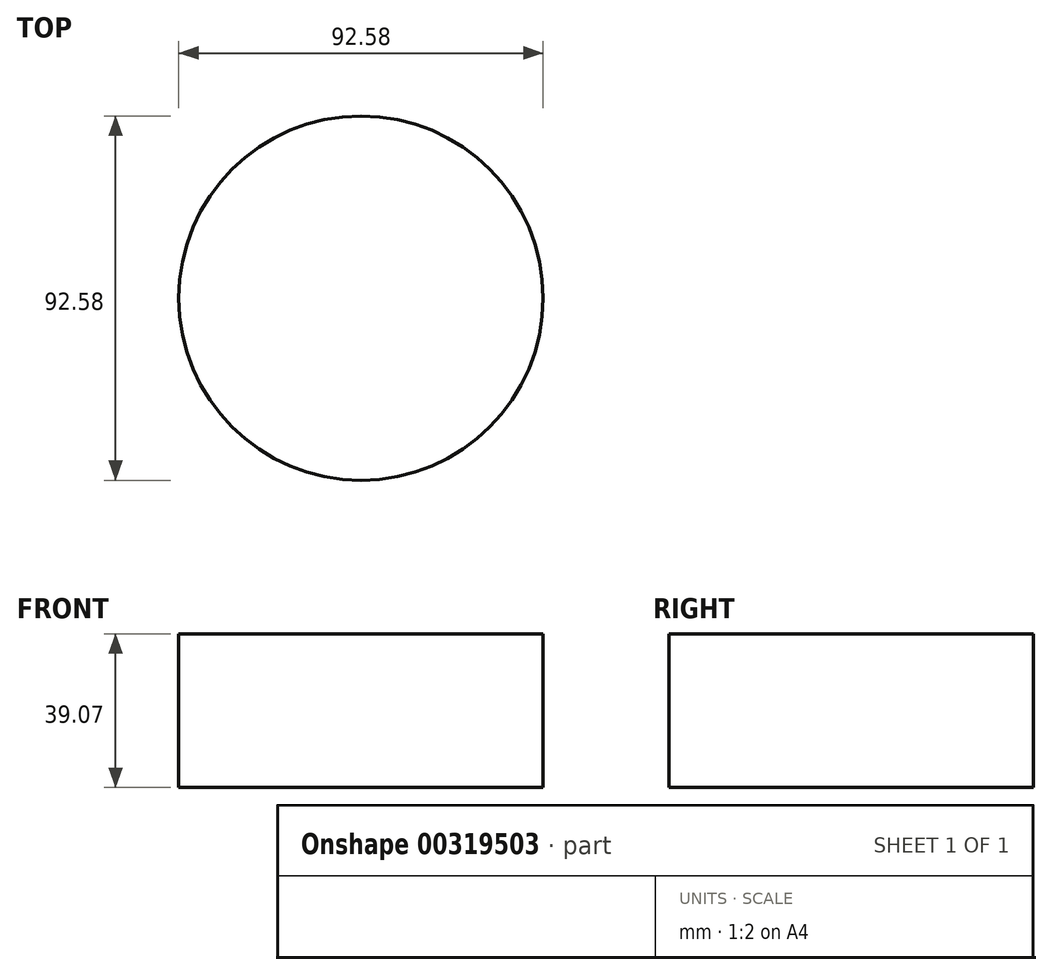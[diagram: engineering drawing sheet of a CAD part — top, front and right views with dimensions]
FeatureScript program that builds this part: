
annotation { "Feature Type Name" : "Feature", "Feature Type Description" : "" }
export const myFeature = defineFeature(function(context is Context, id is Id, definition is map)
    precondition{}
    {
        {
            var Q0;
            Q0=qCreatedBy(makeId("Top.planeOp"),FACE);
            var sketch = newSketch(context, id + "F0", { "sketchPlane" : qUnion([Q0])});
            skCircle(sketch, "E0", {"center": v(0, 0) * mm, "radius": 46.29 * mm});
            skSolve(sketch);
        }
        {
            var Q0;
            Q0 = qSketchRegion(id + "F0", true);
            var sketch = newSketch(context, id + "F1", { "sketchPlane" : qUnion([Q0])});
            skSolve(sketch);
        }
        {
            var Q0;
            Q0 = qSketchRegion(id + "F0", true);
            var Q1;
            Q1=sQuery(id+"F0.wireOp",EDGE,"E0");
            extrude(context, id + "F2", {"entities" : qUnion([Q0]), "bodyType" : ToolBodyType.SURFACE, "surfaceEntities" : qUnion([Q1]), "endBound" : BoundingType.SYMMETRIC, "depth" : 76.2 * mm});
        }
        {
            var Q0;
            Q0=makeQuery(id+"F1.imprint","IMPRINT",FACE,{"disambiguationData":[TD([[makeQuery(id+"F1.imprint","IMPRINT",EDGE,{"derivedFrom":makeQuery(id+"F0.imprint","IMPRINT",EDGE,{"derivedFrom":sQuery(id+"F0.wireOp",EDGE,"E0")})}),1.0]])]});
            extrude(context, id + "F3", {"entities" : qUnion([Q0]), "oppositeDirection" : true, "depth" : 38.43 * mm});
        }
        {
            var Q0;
            Q0=makeQuery(id+"F3.opExtrude","CAP_FACE",FACE,{"disambiguationData":[OSD([sQuery(id+"F0.wireOp",EDGE,"E0")])],"isStart":false});
            extrude(context, id + "F4", {"entities" : qUnion([Q0]), "operationType" : NewBodyOperationType.ADD, "depth" : 0.64 * mm});
        }
    });
